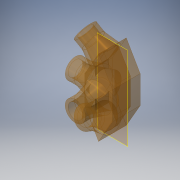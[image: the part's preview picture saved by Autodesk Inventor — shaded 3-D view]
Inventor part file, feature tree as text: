
AUTODESK INVENTOR PART (.ipt)
format: ipt  version: 2016 (Build 200138000, 138)  size: 302,592 bytes
history: native  units: mm
features: extrude x14, sketch x14, plane x1
ambient origin geometry x8: Origin, YZ Plane, XZ Plane, XY Plane, X Axis, Y Axis, Z Axis, Center Point
bodies: Solid1 (feature_tree)
feature tree (29):
  extrude  "Extrusion1"  Depth=30.0mm
  extrude  "Extrusion2"  TaperAngle=120.0deg  [1 undecoded]
  extrude  "Extrusion4"  TaperAngle=120.0deg  [1 undecoded]
  extrude  "Extrusion5"  Depth=30.0mm
  extrude  "Extrusion6"  Depth=10.0mm TaperAngle=0.0deg
  extrude  "Extrusion7"  Depth=15.0mm
  extrude  "Extrusion8"  Depth=15.0mm
  extrude  "Extrusion9"  Depth=15.0mm
  extrude  "Extrusion10"  Depth=15.75mm
  plane  "Work Plane1"
  extrude  "Extrusion11"  Depth=10.0mm TaperAngle=15.0deg
  extrude  "Extrusion12"  Depth=15.0mm TaperAngle=0.0deg
  extrude  "Extrusion13"  Depth=10.0mm TaperAngle=0.0deg
  extrude  "Extrusion14"  Depth=15.75mm
  extrude  "Extrusion15"  Depth=10.0mm
  sketch  "Sketch1"  dims[d6=30.0mm d7=30.0mm]
  sketch  "Sketch2"  dims[d8=30.0mm d9=120.0deg]
  sketch  "Sketch4"  dims[d10=30.0mm d11=120.0deg]
  sketch  "Sketch6"  dims[d12=30.0mm d13=0.0mm d15=30.0mm]
  sketch  "Sketch7"  dims[d16=15.0mm d17=-2.617994mm d23=10.0mm d24=0.0mm]
  sketch  "Sketch8"  dims[d26=30.0mm d27=15.0mm d28=-2.617994mm]
  sketch  "Sketch9"  dims[d29=30.0mm d30=15.0mm d31=-2.617994mm]
  sketch  "Sketch10"  dims[d32=30.0mm d33=15.0mm d34=-2.617994mm]
  sketch  "Sketch11"  dims[d35=25.0mm d36=15.0deg d37=15.75mm]
  sketch  "Sketch12"  dims[d38=10.0mm d39=0.0mm d40=15.0mm d41=15.0deg]
  sketch  "Sketch13"  dims[d42=-15.0mm d43=15.0mm d44=0.0mm]
  sketch  "Sketch14"  dims[d45=15.75mm d46=10.0mm d47=0.0mm]
  sketch  "Sketch15"  dims[d48=15.75mm d49=15.75mm]
  sketch  "Sketch16"  dims[d50=15.0deg d51=15.75mm d52=10.0mm d53=0.0mm d54=15.75mm d55=23.0mm d56=15.0deg]
note: 2 required parameter values undecoded (feature->parameter linkage not recoverable at this tier; creation-order binding heuristic only, values carry confidence <= 0.55)
